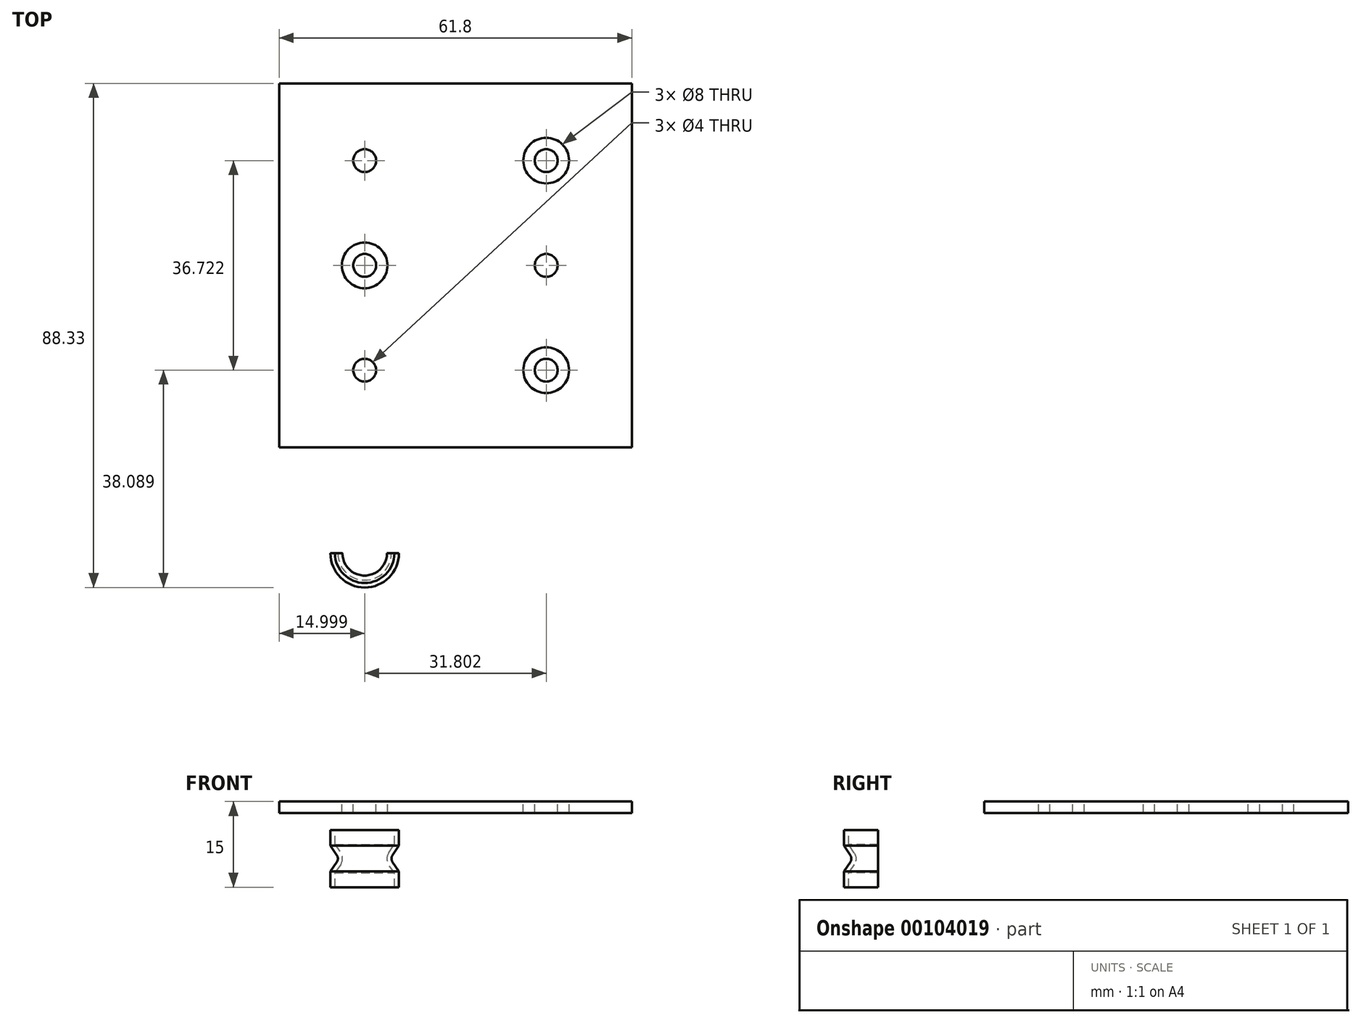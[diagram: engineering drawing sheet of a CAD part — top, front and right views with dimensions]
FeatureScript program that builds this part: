
annotation { "Feature Type Name" : "Feature", "Feature Type Description" : "" }
export const myFeature = defineFeature(function(context is Context, id is Id, definition is map)
    precondition{}
    {
        {
            var Q0;
            Q0=qCreatedBy(makeId("Top.planeOp"),FACE);
            var sketch = newSketch(context, id + "F0", { "sketchPlane" : qUnion([Q0])});
            skLineSegment(sketch, "E0.bottom", {"start": v(-30.9, 50.45) * mm, "end": v(30.9, 50.45) * mm});
            skLineSegment(sketch, "E0.top", {"start": v(-30.9, -50.45) * mm, "end": v(30.9, -50.45) * mm});
            skLineSegment(sketch, "E0.left", {"start": v(-30.9, 50.45) * mm, "end": v(-30.9, -50.45) * mm});
            skLineSegment(sketch, "E0.right", {"start": v(30.9, 50.45) * mm, "end": v(30.9, -50.45) * mm});
            skPoint(sketch, "E0.middle", {"position": v(0, 0) * mm});
            skSolve(sketch);
        }
        {
            var Q0;
            Q0=makeQuery(id+"F0.imprint","IMPRINT",FACE,{"disambiguationData":[TD([[makeQuery(id+"F0.imprint","IMPRINT",EDGE,{"derivedFrom":sQuery(id+"F0.wireOp",EDGE,"E0.bottom")}),-1.0]])]});
            extrude(context, id + "F1", {"entities" : qUnion([Q0]), "depth" : 5 * mm});
        }
        {
            var Q0;
            Q0=makeQuery(id+"F1.opExtrude","SWEPT_FACE",FACE,{"disambiguationData":[OSD([sQuery(id+"F0.wireOp",EDGE,"E0.top")])]});
            var sketch = newSketch(context, id + "F2", { "sketchPlane" : qUnion([Q0])});
            skLineSegment(sketch, "E1", {"start": v(0, 0) * mm, "end": v(0, 5) * mm, "construction": true});
            skCircle(sketch, "E2", {"center": v(-8.4, -5) * mm, "radius": 2.5 * mm, "construction": true});
            skCircle(sketch, "E3.MirrorC", {"center": v(8.4, -5) * mm, "radius": 2.5 * mm, "construction": true});
            skLineSegment(sketch, "E4.bottom", {"start": v(-12.9, 0) * mm, "end": v(-9.9, 0) * mm});
            skLineSegment(sketch, "E4.top", {"start": v(-12.9, -10) * mm, "end": v(-9.9, -10) * mm});
            skLineSegment(sketch, "E4.left", {"start": v(-12.9, 0) * mm, "end": v(-12.9, -10) * mm, "construction": true});
            skLineSegment(sketch, "E4.right", {"start": v(-9.9, 0) * mm, "end": v(-9.9, -2.74) * mm});
            skPoint(sketch, "E4.middle", {"position": v(-11.4, -5) * mm});
            skLineSegment(sketch, "E5", {"start": v(-15.9, 0) * mm, "end": v(-15.9, -10) * mm});
            skLineSegment(sketch, "E6", {"start": v(-11.03, -4.45) * mm, "end": v(-9.9, -2.74) * mm});
            skLineSegment(sketch, "E7", {"start": v(-11.4, -5) * mm, "end": v(-9.9, -5) * mm, "construction": true});
            skLineSegment(sketch, "E8.MirrorCS", {"start": v(-11.03, -5.55) * mm, "end": v(-9.9, -7.26) * mm});
            skLineSegment(sketch, "E9.trimOffspring", {"start": v(-9.9, -7.26) * mm, "end": v(-9.9, -10) * mm});
            skLineSegment(sketch, "E10.0", {"start": v(-10.7, -7.5) * mm, "end": v(-10.7, -10) * mm});
            skLineSegment(sketch, "E10.1", {"start": v(-11.7, -6) * mm, "end": v(-10.7, -7.5) * mm});
            skLineSegment(sketch, "E10.2", {"start": v(-11.7, -4) * mm, "end": v(-10.7, -2.5) * mm});
            skLineSegment(sketch, "E10.3", {"start": v(-10.7, 0) * mm, "end": v(-10.7, -2.5) * mm});
            skPoint(sketch, "E11.visualSharp", {"position": v(-12.36, -5) * mm});
            skArc(sketch, "E11.filletArc", {"start": v(-11.7, -4) * mm, "mid": v(-12, -5) * mm, "end": v(-11.7, -6) * mm});
            skArc(sketch, "E12.filletArc", {"start": v(-11.03, -4.45) * mm, "mid": v(-11.2, -5) * mm, "end": v(-11.03, -5.55) * mm});
            skSolve(sketch);
        }
        {
            var Q0;
            {var subQ1=sQuery(id+"F2.wireOp",EDGE,"E4.bottom");Q0=makeQuery(id+"F2.imprint","IMPRINT",FACE,{"disambiguationData":[TD([[makeQuery(id+"F2.imprint","IMPRINT",EDGE,{"derivedFrom":subQ1}),-1.0]])]});}
            var Q1;
            Q1=sQuery(id+"F2.wireOp",EDGE,"E5");
            revolve(context, id + "F3", {"entities" : qUnion([Q0]), "axis" : qUnion([Q1]), "revolveType" : RevolveType.FULL});
        }
        {
            var Q0;
            Q0=makeQuery(id+"F1.opExtrude","CAP_FACE",FACE,{"disambiguationData":[OSD([sQuery(id+"F0.wireOp",EDGE,"E0.bottom"),sQuery(id+"F0.wireOp",EDGE,"E0.top"),sQuery(id+"F0.wireOp",EDGE,"E0.left"),sQuery(id+"F0.wireOp",EDGE,"E0.right")])],"isStart":false});
            var sketch = newSketch(context, id + "F4", { "sketchPlane" : qUnion([Q0])});
            skPoint(sketch, "E13.0", {"position": v(-15.9, -50.45) * mm});
            skLineSegment(sketch, "E14", {"start": v(0, -50.45) * mm, "end": v(0, 50.45) * mm, "construction": true});
            skCircle(sketch, "E15", {"center": v(-15.9, -18.36) * mm, "radius": 2 * mm});
            skCircle(sketch, "E16.1.0", {"center": v(15.9, 0) * mm, "radius": 2 * mm});
            skCircle(sketch, "E16.2.0", {"center": v(-15.9, 18.36) * mm, "radius": 2 * mm});
            skPoint(sketch, "E16.center", {"position": v(-5.3, 0) * mm});
            skPoint(sketch, "E17.MirrorP", {"position": v(5.3, 0) * mm});
            skCircle(sketch, "E18.MirrorC", {"center": v(15.9, -18.36) * mm, "radius": 2 * mm});
            skCircle(sketch, "E19.MirrorC", {"center": v(-15.9, 0) * mm, "radius": 2 * mm});
            skCircle(sketch, "E20.MirrorC", {"center": v(15.9, 18.36) * mm, "radius": 2 * mm});
            skCircle(sketch, "E21.0", {"center": v(-15.9, 18.36) * mm, "radius": 4 * mm});
            skCircle(sketch, "E22.0", {"center": v(-15.9, -18.36) * mm, "radius": 4 * mm});
            skCircle(sketch, "E23.0", {"center": v(-15.9, 0) * mm, "radius": 4 * mm});
            skCircle(sketch, "E24.MirrorC", {"center": v(15.9, 18.36) * mm, "radius": 4 * mm});
            skCircle(sketch, "E25.MirrorC", {"center": v(15.9, 0) * mm, "radius": 4 * mm});
            skCircle(sketch, "E26.MirrorC", {"center": v(15.9, -18.36) * mm, "radius": 4 * mm});
            skLineSegment(sketch, "E27.bottom", {"start": v(-30.9, -31.88) * mm, "end": v(30.9, -31.88) * mm});
            skLineSegment(sketch, "E27.top", {"start": v(-30.9, 31.88) * mm, "end": v(30.9, 31.88) * mm});
            skLineSegment(sketch, "E27.left", {"start": v(-30.9, -31.88) * mm, "end": v(-30.9, 31.88) * mm});
            skLineSegment(sketch, "E27.right", {"start": v(30.9, -31.88) * mm, "end": v(30.9, 31.88) * mm});
            skPoint(sketch, "E27.middle", {"position": v(0, 0) * mm});
            skSolve(sketch);
        }
        {
            var Q0;
            Q0=makeQuery(id+"F4.imprint","IMPRINT",FACE,{"disambiguationData":[TD([[makeQuery(id+"F4.imprint","IMPRINT",EDGE,{"derivedFrom":sQuery(id+"F4.wireOp",EDGE,"E19.MirrorC")}),-1.0]])]});
            var Q1;
            Q1=makeQuery(id+"F4.imprint","IMPRINT",FACE,{"disambiguationData":[TD([[makeQuery(id+"F4.imprint","IMPRINT",EDGE,{"derivedFrom":sQuery(id+"F4.wireOp",EDGE,"E15")}),1.0]])]});
            var Q2;
            Q2=makeQuery(id+"F4.imprint","IMPRINT",FACE,{"disambiguationData":[TD([[makeQuery(id+"F4.imprint","IMPRINT",EDGE,{"derivedFrom":sQuery(id+"F4.wireOp",EDGE,"E20.MirrorC")}),-1.0]])]});
            var Q3;
            Q3=makeQuery(id+"F4.imprint","IMPRINT",FACE,{"disambiguationData":[TD([[makeQuery(id+"F4.imprint","IMPRINT",EDGE,{"derivedFrom":sQuery(id+"F4.wireOp",EDGE,"E16.1.0")}),1.0]])]});
            var Q4;
            Q4=makeQuery(id+"F4.imprint","IMPRINT",FACE,{"disambiguationData":[TD([[makeQuery(id+"F4.imprint","IMPRINT",EDGE,{"derivedFrom":sQuery(id+"F4.wireOp",EDGE,"E18.MirrorC")}),-1.0]])]});
            var Q5;
            Q5=makeQuery(id+"F4.imprint","IMPRINT",FACE,{"disambiguationData":[TD([[makeQuery(id+"F4.imprint","IMPRINT",EDGE,{"derivedFrom":sQuery(id+"F4.wireOp",EDGE,"E16.2.0")}),1.0]])]});
            var Q6;
            {var subQ0=sQuery(id+"F4.wireOp",EDGE,"E27.top");Q6=makeQuery(id+"F4.imprint","IMPRINT",FACE,{"disambiguationData":[TD([[makeQuery(id+"F4.imprint","IMPRINT",EDGE,{"derivedFrom":subQ0}),1.0]])]});}
            var Q7;
            {var subQ0=sQuery(id+"F4.wireOp",EDGE,"E27.bottom");Q7=makeQuery(id+"F4.imprint","IMPRINT",FACE,{"disambiguationData":[TD([[makeQuery(id+"F4.imprint","IMPRINT",EDGE,{"derivedFrom":subQ0}),-1.0]])]});}
            extrude(context, id + "F5", {"entities" : qUnion([Q0, Q1, Q2, Q3, Q4, Q5, Q6, Q7]), "operationType" : NewBodyOperationType.REMOVE, "oppositeDirection" : true, "depth" : 25 * mm});
        }
        {
            var Q0;
            Q0=makeQuery(id+"F5.boolean.opBoolean","COPY",FACE,{"derivedFrom":makeQuery(id+"F5.opExtrude","SWEPT_FACE",FACE,{"disambiguationData":[OSD([sQuery(id+"F4.wireOp",EDGE,"E27.bottom")])]})});
            var sketch = newSketch(context, id + "F6", { "sketchPlane" : qUnion([Q0])});
            skLineSegment(sketch, "E28", {"start": v(0, 0) * mm, "end": v(0, -7.73) * mm});
            skPoint(sketch, "E28.endSnap0", {"position": v(0, 0) * mm});
            skLineSegment(sketch, "E29.bottom", {"start": v(-30.9, 5) * mm, "end": v(-28.1, 5) * mm});
            skLineSegment(sketch, "E29.top", {"start": v(-30.9, 13) * mm, "end": v(-28.1, 13) * mm});
            skLineSegment(sketch, "E29.left", {"start": v(-30.9, 5) * mm, "end": v(-30.9, 13) * mm});
            skLineSegment(sketch, "E29.right", {"start": v(-28.1, 5) * mm, "end": v(-28.1, 13) * mm});
            skLineSegment(sketch, "E30.MirrorCS", {"start": v(28.1, 5) * mm, "end": v(28.1, 13) * mm});
            skLineSegment(sketch, "E31.MirrorCS", {"start": v(30.9, 13) * mm, "end": v(28.1, 13) * mm});
            skLineSegment(sketch, "E32.MirrorCS", {"start": v(30.9, 5) * mm, "end": v(30.9, 13) * mm});
            skSolve(sketch);
        }
        {
            var Q0;
            Q0=makeQuery(id+"F1.opExtrude","CAP_FACE",FACE,{"disambiguationData":[OSD([sQuery(id+"F0.wireOp",EDGE,"E0.bottom"),sQuery(id+"F0.wireOp",EDGE,"E0.top"),sQuery(id+"F0.wireOp",EDGE,"E0.left"),sQuery(id+"F0.wireOp",EDGE,"E0.right")])],"isStart":true});
            extrude(context, id + "F7", {"entities" : qUnion([Q0]), "operationType" : NewBodyOperationType.REMOVE, "oppositeDirection" : true, "depth" : 3 * mm});
        }
    });
